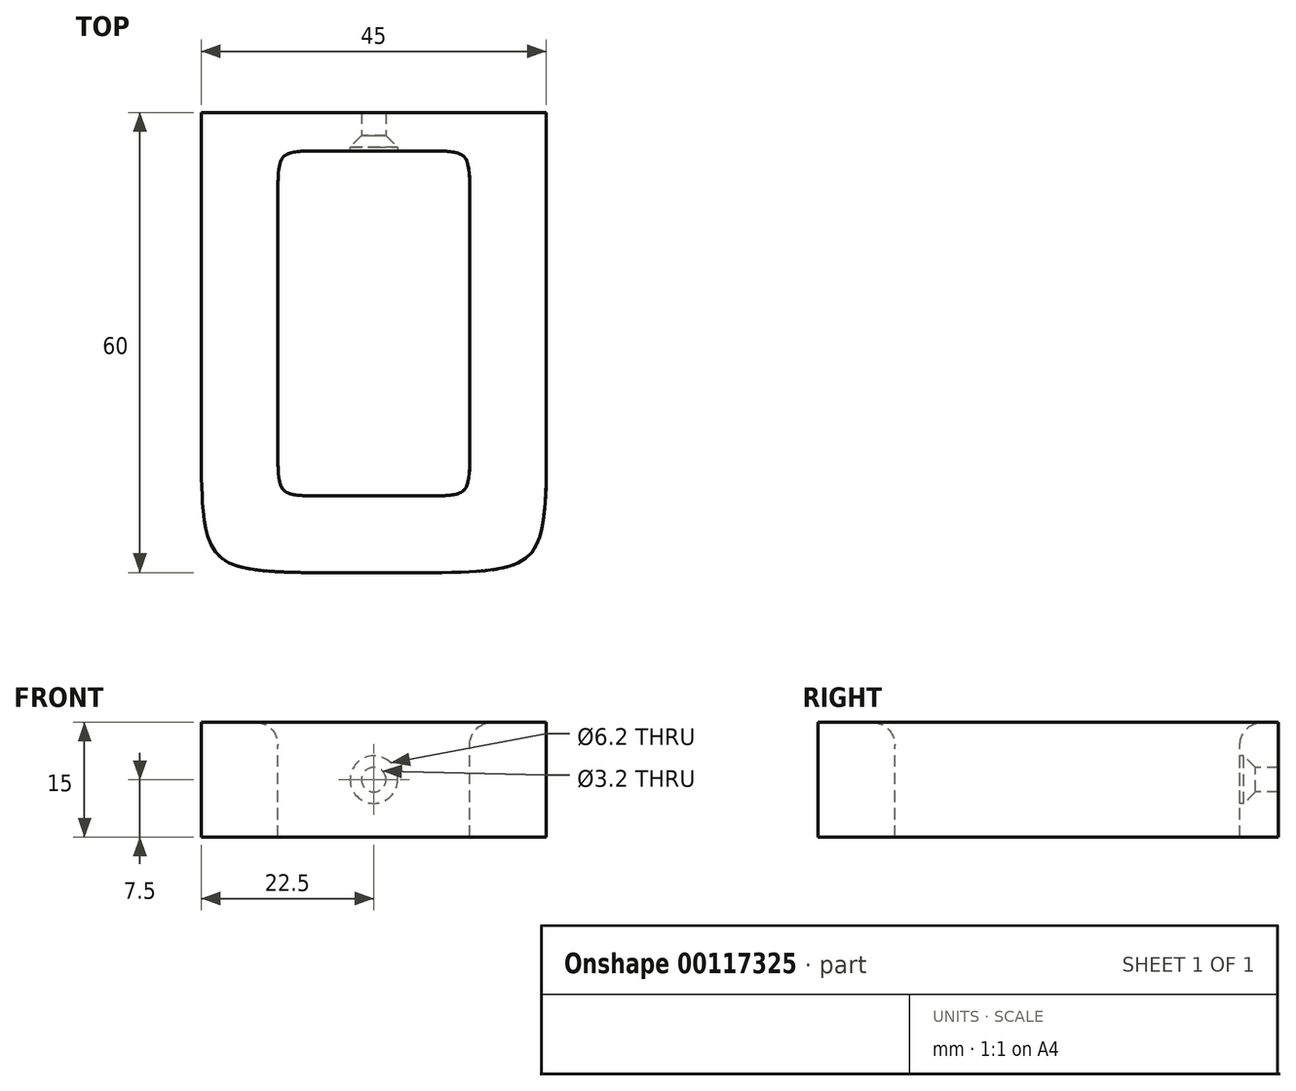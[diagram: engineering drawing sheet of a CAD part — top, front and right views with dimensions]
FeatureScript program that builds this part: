
annotation { "Feature Type Name" : "Feature", "Feature Type Description" : "" }
export const myFeature = defineFeature(function(context is Context, id is Id, definition is map)
    precondition{}
    {
        {
            var Q0;
            Q0=qCreatedBy(makeId("Top.planeOp"),FACE);
            var sketch = newSketch(context, id + "F0", { "sketchPlane" : qUnion([Q0])});
            skLineSegment(sketch, "E0.bottom", {"start": v(-22.5, 0) * mm, "end": v(22.5, 0) * mm});
            skLineSegment(sketch, "E0.top", {"start": v(-22.5, -60) * mm, "end": v(22.5, -60) * mm});
            skLineSegment(sketch, "E0.left", {"start": v(-22.5, 0) * mm, "end": v(-22.5, -60) * mm});
            skLineSegment(sketch, "E0.right", {"start": v(22.5, 0) * mm, "end": v(22.5, -60) * mm});
            skLineSegment(sketch, "E1.bottom", {"start": v(-12.5, -5) * mm, "end": v(12.5, -5) * mm});
            skLineSegment(sketch, "E1.top", {"start": v(-12.5, -50) * mm, "end": v(12.5, -50) * mm});
            skLineSegment(sketch, "E1.left", {"start": v(-12.5, -5) * mm, "end": v(-12.5, -50) * mm});
            skLineSegment(sketch, "E1.right", {"start": v(12.5, -5) * mm, "end": v(12.5, -50) * mm});
            skLineSegment(sketch, "E2", {"start": v(0, -50) * mm, "end": v(0, -60) * mm, "construction": true});
            skLineSegment(sketch, "E3", {"start": v(12.5, -50) * mm, "end": v(22.5, -50) * mm, "construction": true});
            skSolve(sketch);
        }
        {
            var Q0;
            Q0=qSketchRegion(id+"F0",true);
            extrude(context, id + "F1", {"entities" : qUnion([Q0]), "endBound" : BoundingType.SYMMETRIC, "depth" : 15 * mm});
        }
        {
            var Q0;
            Q0=qCreatedBy(makeId("Top.planeOp"),FACE);
            var sketch = newSketch(context, id + "F2", { "sketchPlane" : qUnion([Q0])});
            skLineSegment(sketch, "E4", {"start": v(0, 0) * mm, "end": v(0, -5) * mm});
            skLineSegment(sketch, "E5", {"start": v(0, -5) * mm, "end": v(3.1, -5) * mm});
            skLineSegment(sketch, "E6", {"start": v(3.1, -5) * mm, "end": v(3.1, -4.5) * mm});
            skLineSegment(sketch, "E7", {"start": v(3.1, -4.5) * mm, "end": v(1.6, -3) * mm});
            skLineSegment(sketch, "E8", {"start": v(1.6, -3) * mm, "end": v(1.6, 0) * mm});
            skLineSegment(sketch, "E9", {"start": v(1.6, 0) * mm, "end": v(0, 0) * mm});
            skSolve(sketch);
        }
        {
            var Q0;
            Q0=qSketchRegion(id+"F2",true);
            var Q1;
            Q1=sQuery(id+"F2.wireOp",EDGE,"E4");
            revolve(context, id + "F3", {"operationType" : NewBodyOperationType.REMOVE, "entities" : qUnion([Q0]), "axis" : qUnion([Q1]), "revolveType" : RevolveType.FULL, "oppositeDirection" : true});
        }
        {
            var Q0;
            Q0=makeQuery(id+"F1.opExtrude","SWEPT_EDGE",EDGE,{"disambiguationData":[OSD([sQuery(id+"F0.wireOp",EDGE,"E1.bottom"),sQuery(id+"F0.wireOp",EDGE,"E1.left")])]});
            var Q1;
            Q1=makeQuery(id+"F1.opExtrude","SWEPT_EDGE",EDGE,{"disambiguationData":[OSD([sQuery(id+"F0.wireOp",EDGE,"E1.bottom"),sQuery(id+"F0.wireOp",EDGE,"E1.right")])]});
            var Q2;
            Q2=makeQuery(id+"F1.opExtrude","SWEPT_EDGE",EDGE,{"disambiguationData":[OSD([sQuery(id+"F0.wireOp",EDGE,"E1.top"),sQuery(id+"F0.wireOp",EDGE,"E1.left")])]});
            var Q3;
            Q3=makeQuery(id+"F1.opExtrude","SWEPT_EDGE",EDGE,{"disambiguationData":[OSD([sQuery(id+"F0.wireOp",EDGE,"E1.top"),sQuery(id+"F0.wireOp",EDGE,"E1.right")])]});
            fillet(context, id + "F4", {"entities" : qUnion([Q0, Q1, Q2, Q3]), "radius" : 5 * mm, "tangentPropagation" : true, "rho" : .7, "crossSection" : FilletCrossSection.CONIC, "allowEdgeOverflow" : false});
        }
        {
            var Q0;
            Q0=makeQuery(id+"F1.opExtrude","SWEPT_EDGE",EDGE,{"disambiguationData":[OSD([sQuery(id+"F0.wireOp",EDGE,"E0.top"),sQuery(id+"F0.wireOp",EDGE,"E0.left")])]});
            var Q1;
            Q1=makeQuery(id+"F1.opExtrude","SWEPT_EDGE",EDGE,{"disambiguationData":[OSD([sQuery(id+"F0.wireOp",EDGE,"E0.top"),sQuery(id+"F0.wireOp",EDGE,"E0.right")])]});
            fillet(context, id + "F5", {"entities" : qUnion([Q0, Q1]), "radius" : 15 * mm, "tangentPropagation" : true, "rho" : .7, "crossSection" : FilletCrossSection.CONIC, "allowEdgeOverflow" : false});
        }
        {
            var Q0;
            Q0=makeQuery(id+"F1.opExtrude","CAP_EDGE",EDGE,{"disambiguationData":[OSD([sQuery(id+"F0.wireOp",EDGE,"E1.left")])],"isStart":false});
            var Q1;
            Q1=makeQuery(id+"F1.opExtrude","CAP_EDGE",EDGE,{"disambiguationData":[OSD([sQuery(id+"F0.wireOp",EDGE,"E1.right")])],"isStart":false});
            var Q2;
            {var subQ0=sQuery(id+"F0.wireOp",EDGE,"E1.right");var subQ1=sQuery(id+"F0.wireOp",EDGE,"E1.bottom");Q2=makeQuery(id+"F4.opFillet","BLEND_EDGE",EDGE,{"blendedFrom":[makeQuery(id+"F1.opExtrude","SWEPT_EDGE",EDGE,{"disambiguationData":[OSD([subQ1,subQ0])]}),makeQuery(id+"F1.opExtrude","CAP_FACE",FACE,{"disambiguationData":[OSD([sQuery(id+"F0.wireOp",EDGE,"E0.bottom"),sQuery(id+"F0.wireOp",EDGE,"E0.top"),sQuery(id+"F0.wireOp",EDGE,"E0.left"),sQuery(id+"F0.wireOp",EDGE,"E0.right"),subQ1,sQuery(id+"F0.wireOp",EDGE,"E1.top"),sQuery(id+"F0.wireOp",EDGE,"E1.left"),subQ0])],"isStart":false})],"blendedInto":[makeQuery(id+"F1.opExtrude","CAP_FACE",FACE,{"disambiguationData":[OSD([sQuery(id+"F0.wireOp",EDGE,"E0.bottom"),sQuery(id+"F0.wireOp",EDGE,"E0.top"),sQuery(id+"F0.wireOp",EDGE,"E0.left"),sQuery(id+"F0.wireOp",EDGE,"E0.right"),subQ1,sQuery(id+"F0.wireOp",EDGE,"E1.top"),sQuery(id+"F0.wireOp",EDGE,"E1.left"),subQ0])],"isStart":false})]});}
            var Q3;
            {var subQ0=sQuery(id+"F0.wireOp",EDGE,"E1.left");var subQ1=sQuery(id+"F0.wireOp",EDGE,"E1.bottom");Q3=makeQuery(id+"F4.opFillet","BLEND_EDGE",EDGE,{"blendedFrom":[makeQuery(id+"F1.opExtrude","SWEPT_EDGE",EDGE,{"disambiguationData":[OSD([subQ1,subQ0])]}),makeQuery(id+"F1.opExtrude","CAP_FACE",FACE,{"disambiguationData":[OSD([sQuery(id+"F0.wireOp",EDGE,"E0.bottom"),sQuery(id+"F0.wireOp",EDGE,"E0.top"),sQuery(id+"F0.wireOp",EDGE,"E0.left"),sQuery(id+"F0.wireOp",EDGE,"E0.right"),subQ1,sQuery(id+"F0.wireOp",EDGE,"E1.top"),subQ0,sQuery(id+"F0.wireOp",EDGE,"E1.right")])],"isStart":false})],"blendedInto":[makeQuery(id+"F1.opExtrude","CAP_FACE",FACE,{"disambiguationData":[OSD([sQuery(id+"F0.wireOp",EDGE,"E0.bottom"),sQuery(id+"F0.wireOp",EDGE,"E0.top"),sQuery(id+"F0.wireOp",EDGE,"E0.left"),sQuery(id+"F0.wireOp",EDGE,"E0.right"),subQ1,sQuery(id+"F0.wireOp",EDGE,"E1.top"),subQ0,sQuery(id+"F0.wireOp",EDGE,"E1.right")])],"isStart":false})]});}
            var Q4;
            {var subQ0=sQuery(id+"F0.wireOp",EDGE,"E1.left");var subQ1=sQuery(id+"F0.wireOp",EDGE,"E1.top");Q4=makeQuery(id+"F4.opFillet","BLEND_EDGE",EDGE,{"blendedFrom":[makeQuery(id+"F1.opExtrude","SWEPT_EDGE",EDGE,{"disambiguationData":[OSD([subQ1,subQ0])]}),makeQuery(id+"F1.opExtrude","CAP_FACE",FACE,{"disambiguationData":[OSD([sQuery(id+"F0.wireOp",EDGE,"E0.bottom"),sQuery(id+"F0.wireOp",EDGE,"E0.top"),sQuery(id+"F0.wireOp",EDGE,"E0.left"),sQuery(id+"F0.wireOp",EDGE,"E0.right"),sQuery(id+"F0.wireOp",EDGE,"E1.bottom"),subQ1,subQ0,sQuery(id+"F0.wireOp",EDGE,"E1.right")])],"isStart":false})],"blendedInto":[makeQuery(id+"F1.opExtrude","CAP_FACE",FACE,{"disambiguationData":[OSD([sQuery(id+"F0.wireOp",EDGE,"E0.bottom"),sQuery(id+"F0.wireOp",EDGE,"E0.top"),sQuery(id+"F0.wireOp",EDGE,"E0.left"),sQuery(id+"F0.wireOp",EDGE,"E0.right"),sQuery(id+"F0.wireOp",EDGE,"E1.bottom"),subQ1,subQ0,sQuery(id+"F0.wireOp",EDGE,"E1.right")])],"isStart":false})]});}
            var Q5;
            Q5=makeQuery(id+"F1.opExtrude","CAP_EDGE",EDGE,{"disambiguationData":[OSD([sQuery(id+"F0.wireOp",EDGE,"E1.top")])],"isStart":false});
            var Q6;
            {var subQ0=sQuery(id+"F0.wireOp",EDGE,"E1.right");var subQ1=sQuery(id+"F0.wireOp",EDGE,"E1.top");Q6=makeQuery(id+"F4.opFillet","BLEND_EDGE",EDGE,{"blendedFrom":[makeQuery(id+"F1.opExtrude","SWEPT_EDGE",EDGE,{"disambiguationData":[OSD([subQ1,subQ0])]}),makeQuery(id+"F1.opExtrude","CAP_FACE",FACE,{"disambiguationData":[OSD([sQuery(id+"F0.wireOp",EDGE,"E0.bottom"),sQuery(id+"F0.wireOp",EDGE,"E0.top"),sQuery(id+"F0.wireOp",EDGE,"E0.left"),sQuery(id+"F0.wireOp",EDGE,"E0.right"),sQuery(id+"F0.wireOp",EDGE,"E1.bottom"),subQ1,sQuery(id+"F0.wireOp",EDGE,"E1.left"),subQ0])],"isStart":false})],"blendedInto":[makeQuery(id+"F1.opExtrude","CAP_FACE",FACE,{"disambiguationData":[OSD([sQuery(id+"F0.wireOp",EDGE,"E0.bottom"),sQuery(id+"F0.wireOp",EDGE,"E0.top"),sQuery(id+"F0.wireOp",EDGE,"E0.left"),sQuery(id+"F0.wireOp",EDGE,"E0.right"),sQuery(id+"F0.wireOp",EDGE,"E1.bottom"),subQ1,sQuery(id+"F0.wireOp",EDGE,"E1.left"),subQ0])],"isStart":false})]});}
            fillet(context, id + "F6", {"entities" : qUnion([Q0, Q1, Q2, Q3, Q4, Q5, Q6]), "radius" : 3 * mm, "tangentPropagation" : true, "allowEdgeOverflow" : false});
        }
    });
